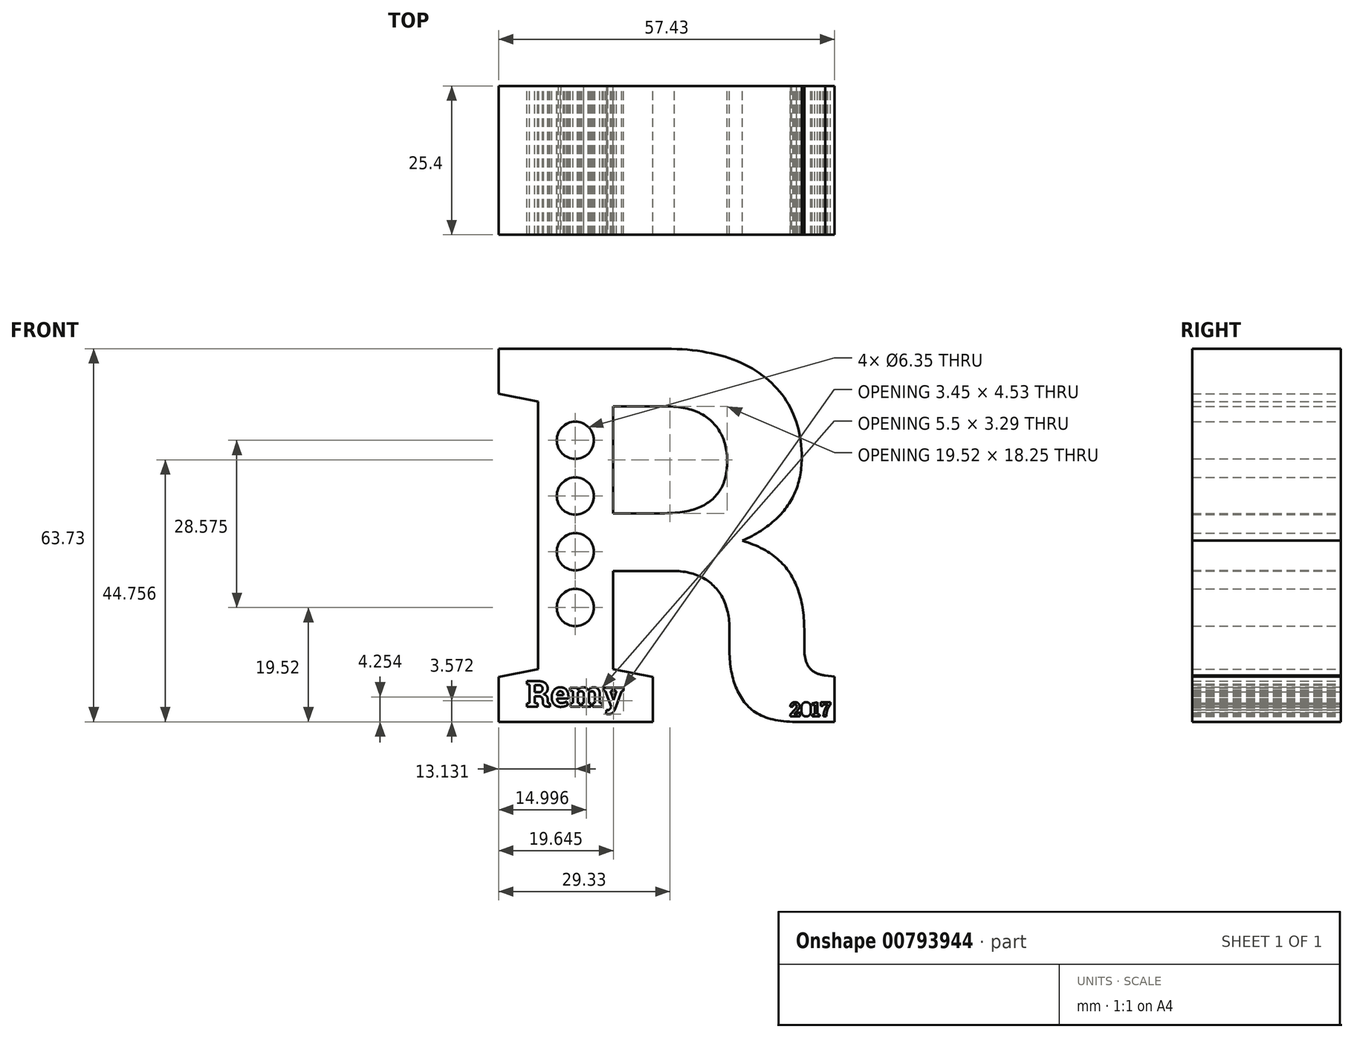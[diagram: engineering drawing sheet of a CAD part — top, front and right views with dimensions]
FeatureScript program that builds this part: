
annotation { "Feature Type Name" : "Feature", "Feature Type Description" : "" }
export const myFeature = defineFeature(function(context is Context, id is Id, definition is map)
    precondition{}
    {
        {
            var Q0;
            Q0=qCreatedBy(makeId("Front.planeOp"),FACE);
            var sketch = newSketch(context, id + "F0", { "sketchPlane" : qUnion([Q0])});
            skText(sketch, "E0", { "text": "R", "fontName": "RobotoSlab-Bold.ttf"});
            const initialGuessF0  = {"E0": [-0.06537, -0.00024, 1, 0, 0.06454]};
            skSetInitialGuess(sketch, initialGuessF0);
            skSolve(sketch);
        }
        {
            var Q0;
            Q0 = qSketchRegion(id + "F0", true);
            extrude(context, id + "F1", {"entities" : qUnion([Q0]), "depth" : 25.4 * mm, "offsetDistance" : 25.4 * mm});
        }
        {
            var Q0;
            Q0=qCreatedBy(makeId("Front.planeOp"),FACE);
            var sketch = newSketch(context, id + "F2", { "sketchPlane" : qUnion([Q0])});
            skCircle(sketch, "E1", {"center": v(-49.79, 47.86) * mm, "radius": 3.18 * mm});
            skCircle(sketch, "E2", {"center": v(-49.79, 38.33) * mm, "radius": 3.18 * mm});
            skCircle(sketch, "E3", {"center": v(-49.79, 28.8) * mm, "radius": 3.18 * mm});
            skCircle(sketch, "E4", {"center": v(-49.79, 19.28) * mm, "radius": 3.18 * mm});
            skSolve(sketch);
        }
        {
            var Q0;
            Q0 = qSketchRegion(id + "F2", true);
            extrude(context, id + "F3", {"entities" : qUnion([Q0]), "operationType" : NewBodyOperationType.REMOVE, "endBound" : BoundingType.THROUGH_ALL, "depth" : 25.4 * mm, "offsetDistance" : 25.4 * mm});
        }
        {
            var Q0;
            Q0=qCreatedBy(makeId("Front.planeOp"),FACE);
            var sketch = newSketch(context, id + "F4", { "sketchPlane" : qUnion([Q0])});
            skText(sketch, "E5", { "text": "Remy", "fontName": "RobotoSlab-Bold.ttf"});
            const initialGuessF4  = {"E5": [-0.05822, 0.00237, 1, 0, 0.0044]};
            skSetInitialGuess(sketch, initialGuessF4);
            skSolve(sketch);
        }
        {
            var Q0;
            Q0 = qSketchRegion(id + "F4", true);
            extrude(context, id + "F5", {"entities" : qUnion([Q0]), "operationType" : NewBodyOperationType.REMOVE, "depth" : 25.4 * mm, "offsetDistance" : 25.4 * mm});
        }
        {
            var Q0;
            Q0=qCreatedBy(makeId("Front.planeOp"),FACE);
            var sketch = newSketch(context, id + "F6", { "sketchPlane" : qUnion([Q0])});
            skText(sketch, "E6", { "text": "2017", "fontName": "RobotoSlab-Bold.ttf"});
            const initialGuessF6  = {"E6": [-0.01314, 0.00071, 1, 0, 0.0024]};
            skSetInitialGuess(sketch, initialGuessF6);
            skSolve(sketch);
        }
        {
            var Q0;
            Q0 = qSketchRegion(id + "F6", true);
            extrude(context, id + "F7", {"entities" : qUnion([Q0]), "operationType" : NewBodyOperationType.REMOVE, "endBound" : BoundingType.THROUGH_ALL, "depth" : 25.4 * mm, "offsetDistance" : 25.4 * mm});
        }
        {
            var Q0;
            Q0=qCreatedBy(makeId("Front.planeOp"),FACE);
            var sketch = newSketch(context, id + "F8", { "sketchPlane" : qUnion([Q0])});
            skSolve(sketch);
        }
        {
            var Q0;
            Q0 = qSketchRegion(id + "F8", true);
            var Q1;
            {var subQ0=sQuery(id+"F0.wireOp",EDGE,"E0.sketch_text.stroke-20");var subQ1=sQuery(id+"F0.wireOp",EDGE,"E0.sketch_text.stroke-19");var subQ2=sQuery(id+"F0.wireOp",EDGE,"E0.sketch_text.stroke-18");var subQ3=sQuery(id+"F0.wireOp",EDGE,"E0.sketch_text.stroke-17");var subQ4=sQuery(id+"F0.wireOp",EDGE,"E0.sketch_text.stroke-16");var subQ5=sQuery(id+"F0.wireOp",EDGE,"E0.sketch_text.stroke-15");var subQ6=sQuery(id+"F0.wireOp",EDGE,"E0.sketch_text.stroke-14");var subQ7=sQuery(id+"F0.wireOp",EDGE,"E0.sketch_text.stroke-13");var subQ8=sQuery(id+"F0.wireOp",EDGE,"E0.sketch_text.stroke-12");var subQ9=sQuery(id+"F0.wireOp",EDGE,"E0.sketch_text.stroke-11");var subQ10=sQuery(id+"F0.wireOp",EDGE,"E0.sketch_text.stroke-10");var subQ11=sQuery(id+"F0.wireOp",EDGE,"E0.sketch_text.stroke-2");var subQ12=sQuery(id+"F0.wireOp",EDGE,"E0.sketch_text.stroke-1");var subQ13=sQuery(id+"F0.wireOp",EDGE,"E0.sketch_text.stroke-3");var subQ14=sQuery(id+"F0.wireOp",EDGE,"E0.sketch_text.stroke-21");var subQ15=sQuery(id+"F0.wireOp",EDGE,"E0.sketch_text.stroke-0");var subQ16=sQuery(id+"F0.wireOp",EDGE,"E0.sketch_text.stroke-9");var subQ17=sQuery(id+"F0.wireOp",EDGE,"E0.sketch_text.stroke-4");var subQ18=sQuery(id+"F0.wireOp",EDGE,"E0.sketch_text.stroke-5");var subQ19=sQuery(id+"F0.wireOp",EDGE,"E0.sketch_text.stroke-6");var subQ20=sQuery(id+"F0.wireOp",EDGE,"E0.sketch_text.stroke-7");var subQ21=sQuery(id+"F0.wireOp",EDGE,"E0.sketch_text.stroke-8");var subQ22=sQuery(id+"F0.wireOp",EDGE,"E0.sketch_text.stroke-35");var subQ23=sQuery(id+"F0.wireOp",EDGE,"E0.sketch_text.stroke-22");var subQ24=sQuery(id+"F0.wireOp",EDGE,"E0.sketch_text.stroke-23");var subQ25=sQuery(id+"F0.wireOp",EDGE,"E0.sketch_text.stroke-24");var subQ26=sQuery(id+"F0.wireOp",EDGE,"E0.sketch_text.stroke-25");var subQ27=sQuery(id+"F0.wireOp",EDGE,"E0.sketch_text.stroke-26");var subQ28=sQuery(id+"F0.wireOp",EDGE,"E0.sketch_text.stroke-28");var subQ29=sQuery(id+"F0.wireOp",EDGE,"E0.sketch_text.stroke-27");var subQ30=sQuery(id+"F0.wireOp",EDGE,"E0.sketch_text.stroke-29");var subQ31=sQuery(id+"F0.wireOp",EDGE,"E0.sketch_text.stroke-30");var subQ32=sQuery(id+"F0.wireOp",EDGE,"E0.sketch_text.stroke-31");var subQ33=sQuery(id+"F0.wireOp",EDGE,"E0.sketch_text.stroke-32");var subQ34=sQuery(id+"F0.wireOp",EDGE,"E0.sketch_text.stroke-33");var subQ35=sQuery(id+"F0.wireOp",EDGE,"E0.sketch_text.stroke-34");Q1=makeQuery(id+"F7.boolean.opBoolean","SPLIT",FACE,{"disambiguationData":[TD([makeQuery(id+"F7.opExtrude","SWEPT_FACE",FACE,{"disambiguationData":[OSD([sQuery(id+"F6.wireOp",EDGE,"E6.sketch_text.stroke-33")])]})])],"derivedFrom":makeQuery(id+"F5.boolean.opBoolean","SPLIT",FACE,{"disambiguationData":[TD([makeQuery(id+"F1.opExtrude","SWEPT_FACE",FACE,{"disambiguationData":[OSD([subQ15])]})])],"derivedFrom":makeQuery(id+"F1.opExtrude","CAP_FACE",FACE,{"disambiguationData":[OSD([subQ15,subQ12,subQ11,subQ13,subQ17,subQ18,subQ19,subQ20,subQ21,subQ16,subQ10,subQ9,subQ8,subQ7,subQ6,subQ5,subQ4,subQ3,subQ2,subQ1,subQ0,subQ14,subQ23,subQ24,subQ25,subQ26,subQ27,subQ29,subQ28,subQ30,subQ31,subQ32,subQ33,subQ34,subQ35,subQ22])],"isStart":false})})});}
            extrude(context, id + "F9", {"entities" : qUnion([Q0, Q1]), "operationType" : NewBodyOperationType.REMOVE, "endBound" : BoundingType.THROUGH_ALL, "oppositeDirection" : true, "depth" : 25.4 * mm, "offsetDistance" : 25.4 * mm});
        }
    });
